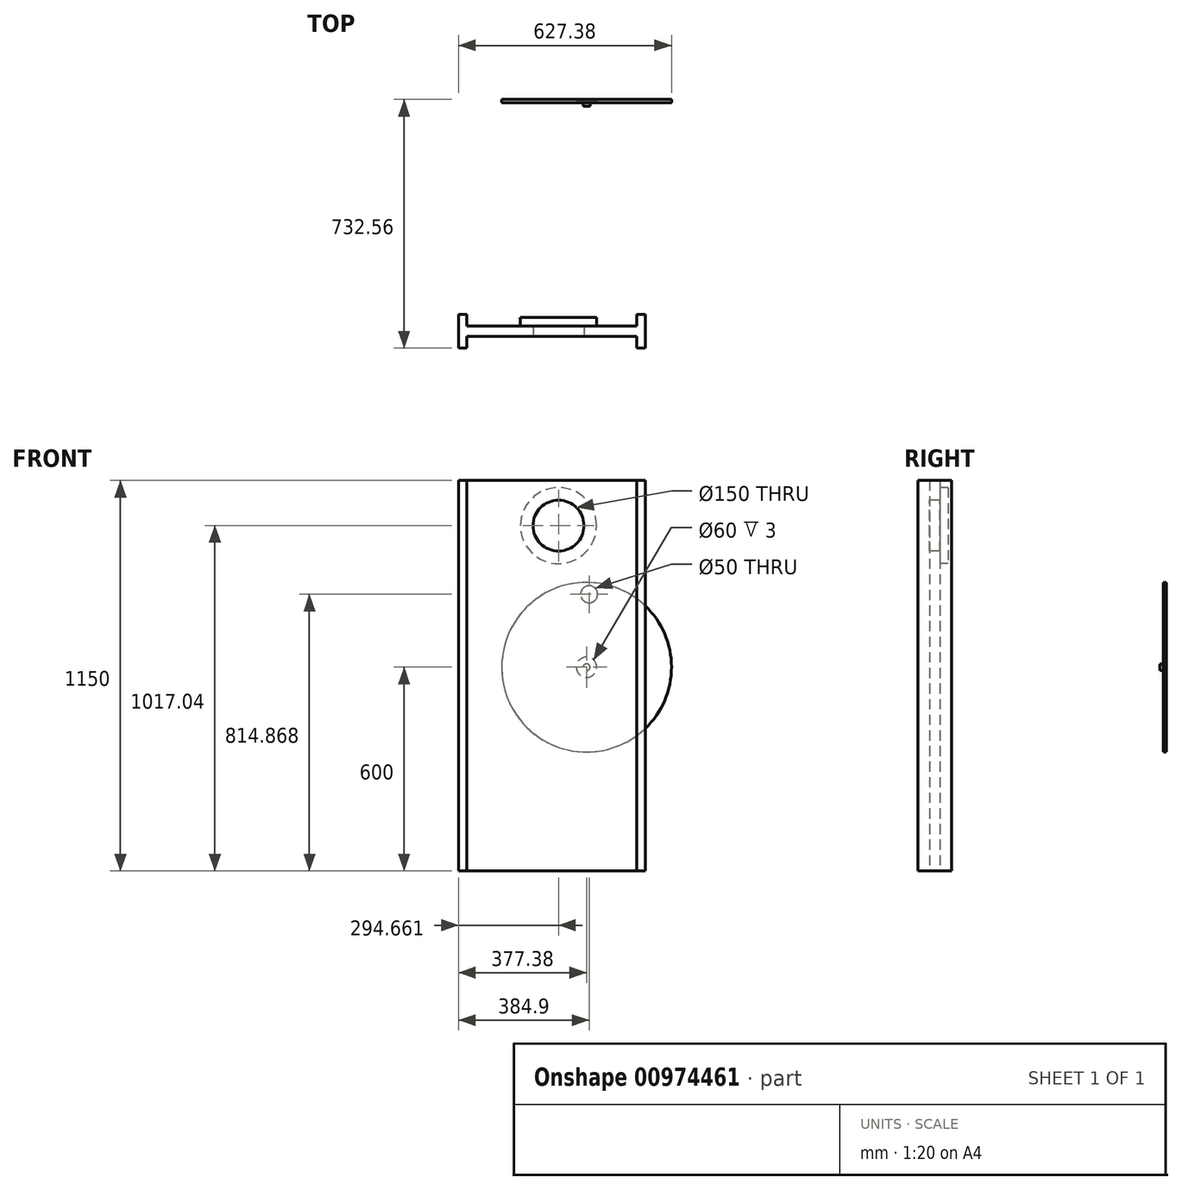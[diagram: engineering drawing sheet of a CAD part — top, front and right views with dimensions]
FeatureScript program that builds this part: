
annotation { "Feature Type Name" : "Feature", "Feature Type Description" : "" }
export const myFeature = defineFeature(function(context is Context, id is Id, definition is map)
    precondition{}
    {
        {
            var Q0;
            Q0=qCreatedBy(makeId("Front.planeOp"),FACE);
            var sketch = newSketch(context, id + "F0", { "sketchPlane" : qUnion([Q0])});
            skCircle(sketch, "E0", {"center": v(130, 600) * mm, "radius": 250 * mm});
            skSolve(sketch);
        }
        {
            var Q0;
            Q0 = qSketchRegion(id + "F0", true);
            extrude(context, id + "F1", {"entities" : qUnion([Q0]), "depth" : 10 * mm, "offsetDistance" : 25 * mm});
        }
        {
            var Q0;
            Q0=makeQuery(id+"F1.opExtrude","CAP_FACE",FACE,{"disambiguationData":[OSD([sQuery(id+"F0.wireOp",EDGE,"E0")])],"isStart":true});
            var sketch = newSketch(context, id + "F2", { "sketchPlane" : qUnion([Q0])});
            skCircle(sketch, "E1", {"center": v(-137.52, 814.87) * mm, "radius": 25 * mm});
            skSolve(sketch);
        }
        {
            var Q0;
            Q0=makeQuery(id+"F1.opExtrude","CAP_FACE",FACE,{"disambiguationData":[OSD([sQuery(id+"F0.wireOp",EDGE,"E0")])],"isStart":false});
            var sketch = newSketch(context, id + "F3", { "sketchPlane" : qUnion([Q0])});
            skCircle(sketch, "E2", {"center": v(130, 600) * mm, "radius": 10 * mm});
            skSolve(sketch);
        }
        {
            var Q0;
            Q0=makeQuery(id+"F3.imprint","IMPRINT",FACE,{"disambiguationData":[TD([[makeQuery(id+"F3.imprint","IMPRINT",EDGE,{"derivedFrom":sQuery(id+"F3.wireOp",EDGE,"E2")}),1.0]])]});
            extrude(context, id + "F4", {"entities" : qUnion([Q0]), "operationType" : NewBodyOperationType.ADD, "depth" : 10 * mm, "offsetDistance" : 25 * mm});
        }
        {
            var Q0;
            Q0=makeQuery(id+"F1.opExtrude","CAP_FACE",FACE,{"disambiguationData":[OSD([sQuery(id+"F0.wireOp",EDGE,"E0")])],"isStart":true});
            var sketch = newSketch(context, id + "F5", { "sketchPlane" : qUnion([Q0])});
            skCircle(sketch, "E3", {"center": v(-130, 600) * mm, "radius": 30 * mm});
            skSolve(sketch);
        }
        {
            var Q0;
            Q0=makeQuery(id+"F5.imprint","IMPRINT",FACE,{"disambiguationData":[TD([[makeQuery(id+"F5.imprint","IMPRINT",EDGE,{"derivedFrom":sQuery(id+"F5.wireOp",EDGE,"E3")}),1.0]])]});
            var Q1;
            Q1=sQuery(id+"F5.wireOp",EDGE,"E3");
            extrude(context, id + "F6", {"entities" : qUnion([Q0]), "operationType" : NewBodyOperationType.REMOVE, "surfaceEntities" : qUnion([Q1]), "oppositeDirection" : true, "depth" : 3 * mm, "offsetDistance" : 25 * mm});
        }
        {
            var Q0;
            Q0=makeQuery(id+"F2.imprint","IMPRINT",FACE,{"disambiguationData":[TD([[makeQuery(id+"F2.imprint","IMPRINT",EDGE,{"derivedFrom":sQuery(id+"F2.wireOp",EDGE,"E1")}),1.0]])]});
            var Q1;
            Q1=sQuery(id+"F2.wireOp",EDGE,"E1");
            extrude(context, id + "F7", {"entities" : qUnion([Q0]), "operationType" : NewBodyOperationType.REMOVE, "surfaceEntities" : qUnion([Q1]), "endBound" : BoundingType.UP_TO_NEXT, "oppositeDirection" : true, "depth" : 25 * mm, "offsetDistance" : 25 * mm});
        }
        {
            var Q0;
            Q0=qCreatedBy(makeId("Top.planeOp"),FACE);
            var sketch = newSketch(context, id + "F8", { "sketchPlane" : qUnion([Q0])});
            skLineSegment(sketch, "E4", {"start": v(-247.38, -632.56) * mm, "end": v(-247.38, -732.56) * mm});
            skLineSegment(sketch, "E5", {"start": v(-247.38, -732.56) * mm, "end": v(-222.38, -732.56) * mm});
            skLineSegment(sketch, "E6", {"start": v(-222.38, -732.56) * mm, "end": v(-222.38, -697.56) * mm});
            skLineSegment(sketch, "E7", {"start": v(-222.38, -697.56) * mm, "end": v(277.62, -697.56) * mm});
            skLineSegment(sketch, "E8", {"start": v(277.62, -697.56) * mm, "end": v(277.62, -732.56) * mm});
            skLineSegment(sketch, "E9", {"start": v(277.62, -732.56) * mm, "end": v(302.62, -732.56) * mm});
            skLineSegment(sketch, "E10", {"start": v(302.62, -732.56) * mm, "end": v(302.62, -632.56) * mm});
            skLineSegment(sketch, "E11", {"start": v(302.62, -632.56) * mm, "end": v(277.62, -632.56) * mm});
            skLineSegment(sketch, "E12", {"start": v(277.62, -632.56) * mm, "end": v(277.62, -667.56) * mm});
            skLineSegment(sketch, "E13", {"start": v(277.62, -667.56) * mm, "end": v(-222.38, -667.56) * mm});
            skLineSegment(sketch, "E14", {"start": v(-222.38, -667.56) * mm, "end": v(-222.38, -632.56) * mm});
            skLineSegment(sketch, "E15", {"start": v(-222.38, -632.56) * mm, "end": v(-247.38, -632.56) * mm});
            skSolve(sketch);
        }
        {
            var Q0;
            Q0=makeQuery(id+"F8.imprint","IMPRINT",FACE,{"disambiguationData":[TD([[makeQuery(id+"F8.imprint","IMPRINT",EDGE,{"derivedFrom":sQuery(id+"F8.wireOp",EDGE,"E4")}),1.0]])]});
            extrude(context, id + "F9", {"entities" : qUnion([Q0]), "depth" : 1150 * mm, "offsetDistance" : 25 * mm});
        }
        {
            var Q0;
            Q0=makeQuery(id+"F9.opExtrude","SWEPT_FACE",FACE,{"disambiguationData":[OSD([sQuery(id+"F8.wireOp",EDGE,"E7")])]});
            var sketch = newSketch(context, id + "F10", { "sketchPlane" : qUnion([Q0])});
            skCircle(sketch, "E16", {"center": v(47.28, 1017.05) * mm, "radius": 75 * mm});
            skSolve(sketch);
        }
        {
            var Q0;
            Q0 = qSketchRegion(id + "F10", true);
            extrude(context, id + "F11", {"entities" : qUnion([Q0]), "operationType" : NewBodyOperationType.REMOVE, "endBound" : BoundingType.UP_TO_NEXT, "oppositeDirection" : true, "depth" : 25 * mm, "offsetDistance" : 25 * mm});
        }
        {
            var Q0;
            Q0=makeQuery(id+"F9.opExtrude","SWEPT_FACE",FACE,{"disambiguationData":[OSD([sQuery(id+"F8.wireOp",EDGE,"E13")])]});
            var sketch = newSketch(context, id + "F12", { "sketchPlane" : qUnion([Q0])});
            skCircle(sketch, "E17", {"center": v(-47.28, 1017.05) * mm, "radius": 112.03 * mm});
            skSolve(sketch);
        }
        {
            var Q0;
            Q0 = qSketchRegion(id + "F12", true);
            extrude(context, id + "F13", {"entities" : qUnion([Q0]), "depth" : 25 * mm, "offsetDistance" : 25 * mm});
        }
    });
